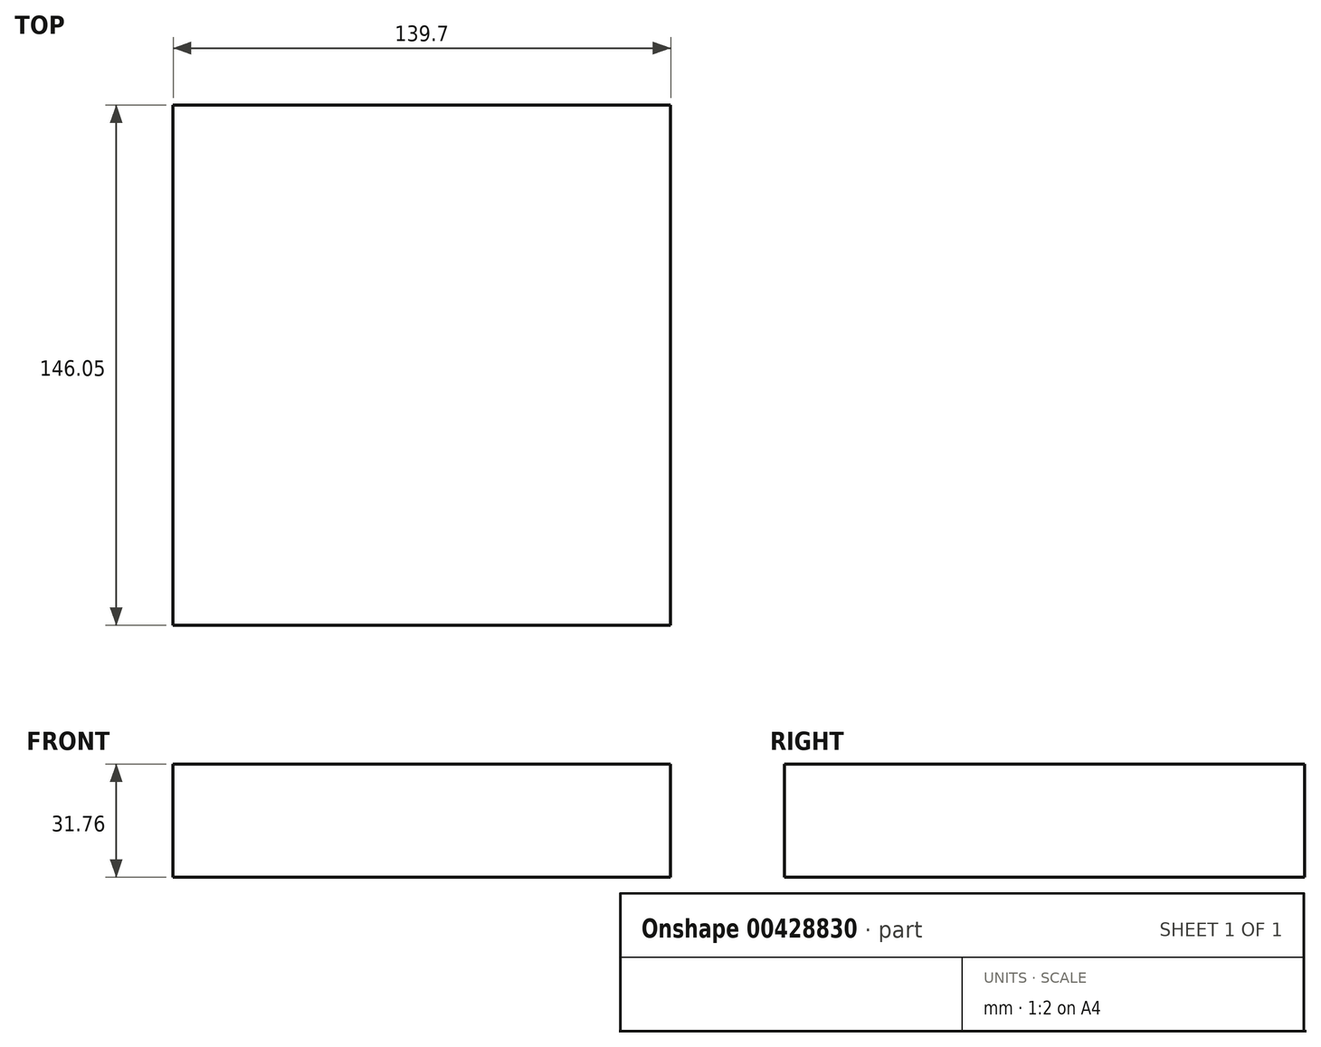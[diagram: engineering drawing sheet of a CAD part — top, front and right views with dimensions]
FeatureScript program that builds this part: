
annotation { "Feature Type Name" : "Feature", "Feature Type Description" : "" }
export const myFeature = defineFeature(function(context is Context, id is Id, definition is map)
    precondition{}
    {
        {
            var Q0;
            Q0=qCreatedBy(makeId("Top.planeOp"),FACE);
            var sketch = newSketch(context, id + "F0", { "sketchPlane" : qUnion([Q0])});
            skLineSegment(sketch, "E0.bottom", {"start": v(-60.96, -73.28) * mm, "end": v(78.74, -73.28) * mm});
            skLineSegment(sketch, "E0.top", {"start": v(-60.96, 72.77) * mm, "end": v(78.74, 72.77) * mm});
            skLineSegment(sketch, "E0.left", {"start": v(-60.96, -73.28) * mm, "end": v(-60.96, 72.77) * mm});
            skLineSegment(sketch, "E0.right", {"start": v(78.74, -73.28) * mm, "end": v(78.74, 72.77) * mm});
            skSolve(sketch);
        }
        {
            var Q0;
            Q0=makeQuery(id+"F0.imprint","IMPRINT",FACE,{"disambiguationData":[TD([[makeQuery(id+"F0.imprint","IMPRINT",EDGE,{"derivedFrom":sQuery(id+"F0.wireOp",EDGE,"E0.bottom")}),1.0]])]});
            extrude(context, id + "F1", {"entities" : qUnion([Q0]), "endBound" : BoundingType.SYMMETRIC, "depth" : 31.75 * mm});
        }
    });
